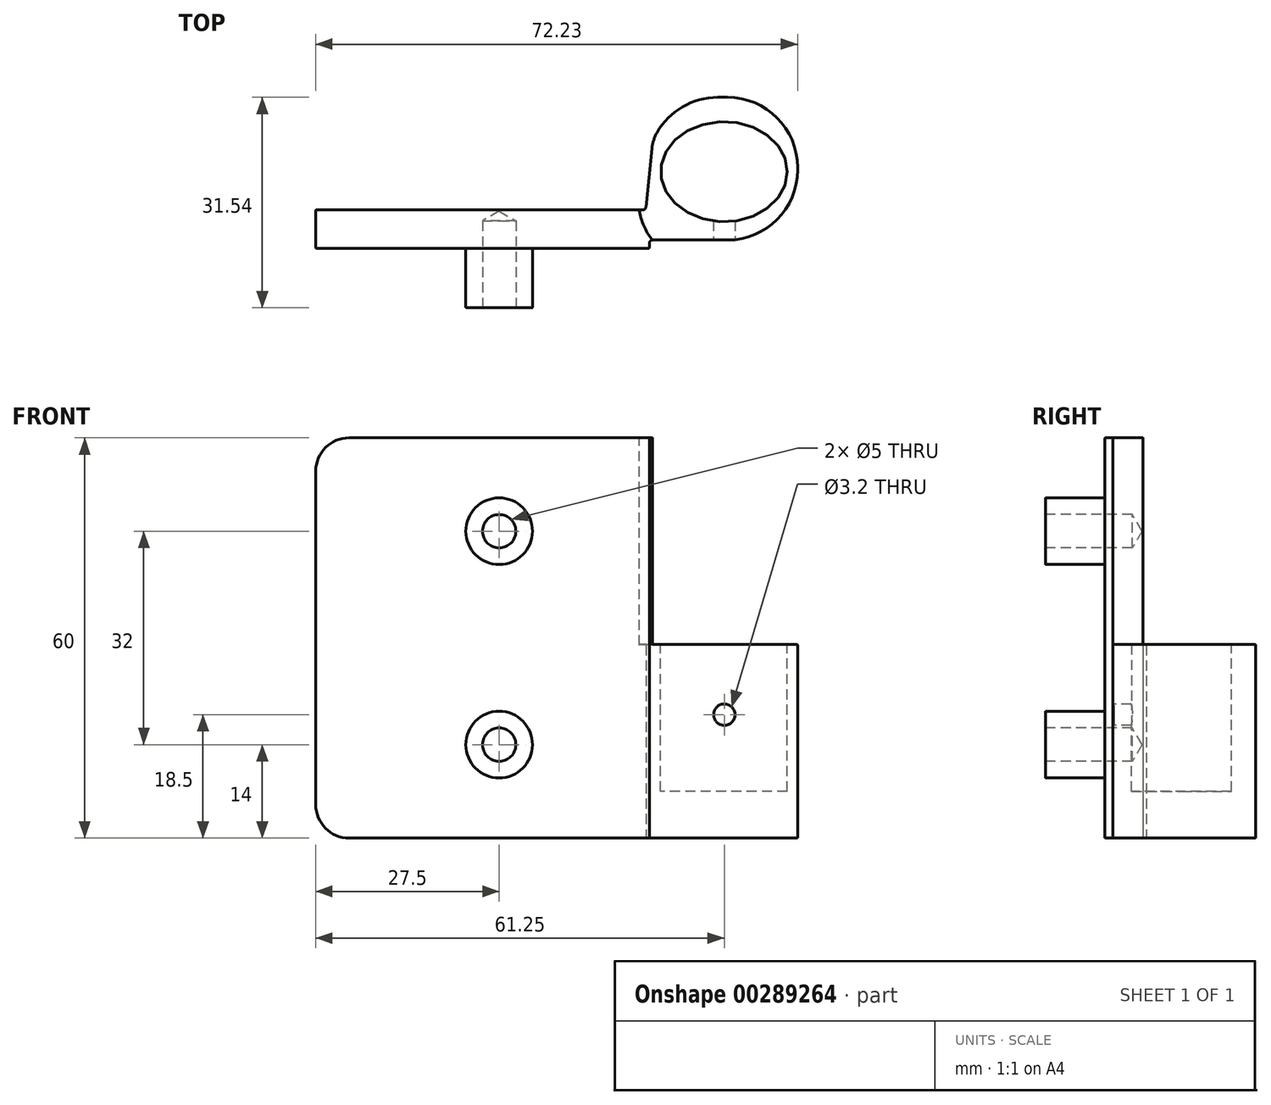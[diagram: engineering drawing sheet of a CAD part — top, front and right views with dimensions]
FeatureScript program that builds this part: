
annotation { "Feature Type Name" : "Feature", "Feature Type Description" : "" }
export const myFeature = defineFeature(function(context is Context, id is Id, definition is map)
    precondition{}
    {
        {
            var Q0;
            Q0=qCreatedBy(makeId("Front.planeOp"),FACE);
            var sketch = newSketch(context, id + "F0", { "sketchPlane" : qUnion([Q0])});
            skLineSegment(sketch, "E0", {"start": v(0, 0) * mm, "end": v(-48.5, 0) * mm});
            skLineSegment(sketch, "E1", {"start": v(-48.5, 0) * mm, "end": v(-48.5, -5.75) * mm});
            skLineSegment(sketch, "E2", {"start": v(-48.5, -5.75) * mm, "end": v(1.5, -5.75) * mm});
            skLineSegment(sketch, "E3", {"start": v(1.5, -5.75) * mm, "end": v(1.5, -5) * mm});
            skLineSegment(sketch, "E4", {"start": v(2, -4.5) * mm, "end": v(3.23, -4.5) * mm});
            skLineSegment(sketch, "E5", {"start": v(3.23, -4.5) * mm, "end": v(13.23, -4.5) * mm});
            skLineSegment(sketch, "E6", {"start": v(23.73, 6) * mm, "end": v(23.73, 6.4) * mm});
            skLineSegment(sketch, "E7", {"start": v(13.23, 16.9) * mm, "end": v(11.78, 16.9) * mm});
            skLineSegment(sketch, "E8", {"start": v(0.5, 0) * mm, "end": v(0, 0) * mm});
            skArc(sketch, "E9.filletArc", {"start": v(13.23, -4.5) * mm, "mid": v(20.66, -1.43) * mm, "end": v(23.73, 6) * mm});
            skArc(sketch, "E10.filletArc", {"start": v(23.73, 6.4) * mm, "mid": v(20.66, 13.82) * mm, "end": v(13.23, 16.9) * mm});
            skArc(sketch, "E11.filletArc", {"start": v(11.78, 16.9) * mm, "mid": v(6.5, 15.47) * mm, "end": v(2.65, 11.6) * mm});
            skArc(sketch, "E12.filletArc", {"start": v(0.5, 0) * mm, "mid": v(0.85, 0.15) * mm, "end": v(1, 0.5) * mm});
            skPoint(sketch, "E13.visualSharp", {"position": v(1.5, -4.5) * mm});
            skArc(sketch, "E13.filletArc", {"start": v(2, -4.5) * mm, "mid": v(1.65, -4.66) * mm, "end": v(1.5, -5) * mm});
            skLineSegment(sketch, "E14", {"start": v(1, 0.5) * mm, "end": v(1.9, 9.23) * mm});
            skPoint(sketch, "E15.visualSharp", {"position": v(2, 10.22) * mm});
            skArc(sketch, "E15.filletArc", {"start": v(2.65, 11.6) * mm, "mid": v(2.15, 10.45) * mm, "end": v(1.9, 9.23) * mm});
            skSolve(sketch);
        }
        {
            var Q0;
            Q0=makeQuery(id+"F0.imprint","IMPRINT",FACE,{"disambiguationData":[TD([[makeQuery(id+"F0.imprint","IMPRINT",EDGE,{"derivedFrom":sQuery(id+"F0.wireOp",EDGE,"E0")}),1.0]])]});
            extrude(context, id + "F1", {"entities" : qUnion([Q0]), "depth" : 60 * mm});
        }
        {
            var Q0;
            Q0=makeQuery(id+"F1.opExtrude","CAP_EDGE",EDGE,{"disambiguationData":[OSD([sQuery(id+"F0.wireOp",EDGE,"E1")])],"isStart":false});
            var Q1;
            Q1=makeQuery(id+"F1.opExtrude","CAP_EDGE",EDGE,{"disambiguationData":[OSD([sQuery(id+"F0.wireOp",EDGE,"E1")])],"isStart":true});
            fillet(context, id + "F2", {"entities" : qUnion([Q0, Q1]), "radius" : 5 * mm, "tangentPropagation" : true, "allowEdgeOverflow" : false});
        }
        {
            var Q0;
            Q0=makeQuery(id+"F1.opExtrude","SWEPT_FACE",FACE,{"disambiguationData":[OSD([sQuery(id+"F0.wireOp",EDGE,"E4"),sQuery(id+"F0.wireOp",EDGE,"E5")])]});
            var sketch = newSketch(context, id + "F3", { "sketchPlane" : qUnion([Q0])});
            skLineSegment(sketch, "E16.bottom", {"start": v(2, 60) * mm, "end": v(31.94, 60) * mm});
            skLineSegment(sketch, "E16.top", {"start": v(2, 29) * mm, "end": v(31.94, 29) * mm});
            skLineSegment(sketch, "E16.left", {"start": v(2, 60) * mm, "end": v(2, 29) * mm});
            skLineSegment(sketch, "E16.right", {"start": v(31.94, 60) * mm, "end": v(31.94, 29) * mm});
            skSolve(sketch);
        }
        {
            var Q0;
            Q0 = qSketchRegion(id + "F3", true);
            extrude(context, id + "F4", {"entities" : qUnion([Q0]), "operationType" : NewBodyOperationType.REMOVE, "endBound" : BoundingType.THROUGH_ALL, "oppositeDirection" : true, "depth" : 25 * mm});
        }
        {
            var Q0;
            Q0=makeQuery(id+"F1.opExtrude","CAP_FACE",FACE,{"disambiguationData":[OSD([sQuery(id+"F0.wireOp",EDGE,"E0"),sQuery(id+"F0.wireOp",EDGE,"E1"),sQuery(id+"F0.wireOp",EDGE,"E2"),sQuery(id+"F0.wireOp",EDGE,"E3"),sQuery(id+"F0.wireOp",EDGE,"E4"),sQuery(id+"F0.wireOp",EDGE,"E5"),sQuery(id+"F0.wireOp",EDGE,"E6"),sQuery(id+"F0.wireOp",EDGE,"E7"),sQuery(id+"F0.wireOp",EDGE,"GG9Xp7Lx-0V8L-KjhP-dehT-RjXL1Wiv3JEy"),sQuery(id+"F0.wireOp",EDGE,"E8"),sQuery(id+"F0.wireOp",EDGE,"E9.filletArc"),sQuery(id+"F0.wireOp",EDGE,"E10.filletArc"),sQuery(id+"F0.wireOp",EDGE,"E11.filletArc"),sQuery(id+"F0.wireOp",EDGE,"E12.filletArc"),sQuery(id+"F0.wireOp",EDGE,"E13.filletArc")])],"isStart":false});
            var sketch = newSketch(context, id + "F5", { "sketchPlane" : qUnion([Q0])});
            skArc(sketch, "E17", {"start": v(0, 0) * mm, "mid": v(0.68, -2.4) * mm, "end": v(2, -4.5) * mm});
            skLineSegment(sketch, "E18", {"start": v(2, -4.5) * mm, "end": v(4.6, -0.03) * mm});
            skLineSegment(sketch, "E19", {"start": v(4.6, -0.03) * mm, "end": v(2.71, 13.2) * mm});
            skLineSegment(sketch, "E20", {"start": v(2.71, 13.2) * mm, "end": v(-1.4, 7.63) * mm});
            skLineSegment(sketch, "E21", {"start": v(0, 0) * mm, "end": v(-1.4, 7.63) * mm});
            skSolve(sketch);
        }
        {
            var Q0;
            Q0 = qSketchRegion(id + "F5", true);
            extrude(context, id + "F6", {"entities" : qUnion([Q0]), "operationType" : NewBodyOperationType.REMOVE, "oppositeDirection" : true, "depth" : 31 * mm});
        }
        {
            var Q0;
            Q0=makeQuery(id+"F1.opExtrude","SWEPT_BODY",BODY,{"disambiguationData":[OSD([sQuery(id+"F0.wireOp",EDGE,"E0"),sQuery(id+"F0.wireOp",EDGE,"E1"),sQuery(id+"F0.wireOp",EDGE,"E2"),sQuery(id+"F0.wireOp",EDGE,"E3"),sQuery(id+"F0.wireOp",EDGE,"E4"),sQuery(id+"F0.wireOp",EDGE,"E5"),sQuery(id+"F0.wireOp",EDGE,"E6"),sQuery(id+"F0.wireOp",EDGE,"E7"),sQuery(id+"F0.wireOp",EDGE,"GG9Xp7Lx-0V8L-KjhP-dehT-RjXL1Wiv3JEy"),sQuery(id+"F0.wireOp",EDGE,"E8"),sQuery(id+"F0.wireOp",EDGE,"E9.filletArc"),sQuery(id+"F0.wireOp",EDGE,"E10.filletArc"),sQuery(id+"F0.wireOp",EDGE,"E11.filletArc"),sQuery(id+"F0.wireOp",EDGE,"E12.filletArc"),sQuery(id+"F0.wireOp",EDGE,"E13.filletArc")])]});
            var Q1;
            Q1=makeQuery(id+"F1.opExtrude","CAP_EDGE",EDGE,{"disambiguationData":[OSD([sQuery(id+"F0.wireOp",EDGE,"E0"),sQuery(id+"F0.wireOp",EDGE,"E8")])],"isStart":true});
            transform(context, id + "F7", {"entities" : qUnion([Q0]), "transformType" : TransformType.ROTATION, "transformAxis" : qUnion([Q1]), "angle" : 90 * degree, "makeCopy" : false});
        }
        {
            var Q0;
            Q0=makeQuery(id+"F1.opExtrude","SWEPT_FACE",FACE,{"disambiguationData":[OSD([sQuery(id+"F0.wireOp",EDGE,"E2")])]});
            var sketch = newSketch(context, id + "F8", { "sketchPlane" : qUnion([Q0])});
            skCircle(sketch, "E22", {"center": v(-21, 46) * mm, "radius": 5 * mm});
            skCircle(sketch, "E23", {"center": v(-21, 14) * mm, "radius": 5 * mm});
            skSolve(sketch);
        }
        {
            var Q0;
            Q0 = qSketchRegion(id + "F8", true);
            extrude(context, id + "F9", {"entities" : qUnion([Q0]), "operationType" : NewBodyOperationType.ADD, "depth" : 8.9 * mm});
        }
        {
            var Q0;
            Q0=makeQuery(id+"F9.opExtrude","CAP_FACE",FACE,{"disambiguationData":[OSD([sQuery(id+"F8.wireOp",EDGE,"E22")])],"isStart":false});
            var sketch = newSketch(context, id + "F10", { "sketchPlane" : qUnion([Q0])});
            skCircle(sketch, "E24", {"center": v(-21, 46) * mm, "radius": 2.5 * mm});
            skSolve(sketch);
        }
        {
            var Q0;
            Q0=makeQuery(id+"F9.opExtrude","CAP_FACE",FACE,{"disambiguationData":[OSD([sQuery(id+"F8.wireOp",EDGE,"E23")])],"isStart":false});
            var sketch = newSketch(context, id + "F11", { "sketchPlane" : qUnion([Q0])});
            skCircle(sketch, "E25", {"center": v(-21, 14) * mm, "radius": 2.5 * mm});
            skSolve(sketch);
        }
        {
            var Q0;
            Q0=sQuery(id+"F10.wireOp",VERTEX,"E24.center");
            var Q1;
            Q1=makeQuery(id+"F1.opExtrude","SWEPT_BODY",BODY,{"disambiguationData":[OSD([sQuery(id+"F0.wireOp",EDGE,"E0"),sQuery(id+"F0.wireOp",EDGE,"E1"),sQuery(id+"F0.wireOp",EDGE,"E2"),sQuery(id+"F0.wireOp",EDGE,"E3"),sQuery(id+"F0.wireOp",EDGE,"E4"),sQuery(id+"F0.wireOp",EDGE,"E5"),sQuery(id+"F0.wireOp",EDGE,"E6"),sQuery(id+"F0.wireOp",EDGE,"E7"),sQuery(id+"F0.wireOp",EDGE,"GG9Xp7Lx-0V8L-KjhP-dehT-RjXL1Wiv3JEy"),sQuery(id+"F0.wireOp",EDGE,"E8"),sQuery(id+"F0.wireOp",EDGE,"E9.filletArc"),sQuery(id+"F0.wireOp",EDGE,"E10.filletArc"),sQuery(id+"F0.wireOp",EDGE,"E11.filletArc"),sQuery(id+"F0.wireOp",EDGE,"E12.filletArc"),sQuery(id+"F0.wireOp",EDGE,"E13.filletArc")])]});
            hole(context, id + "F12", {"style" : HoleStyle.SIMPLE, "endStyle" : HoleEndStyle.BLIND, "standardTappedOrClearance" : lookupTablePath({ "standard" : "ISO", "engagement" : "75%", "pitch" : "1 mm", "size" : "M6", "type" : "Tapped" }), "standardBlindInLast" : lookupTablePath({ "standard" : "ISO", "engagement" : "75%", "pitch" : "1 mm", "size" : "M6", "type" : "Tapped" }), "holeDiameter" : 5 * mm, "showTappedDepth" : true, "holeDepth" : 13 * mm, "tappedDepth" : 10 * mm, "tapClearance" : 3, "locations" : qUnion([Q0]), "scope" : qUnion([Q1]), "majorDiameter" : 6 * mm});
        }
        {
            var Q0;
            Q0=sQuery(id+"F11.wireOp",VERTEX,"E25.center");
            var Q1;
            Q1=makeQuery(id+"F1.opExtrude","SWEPT_BODY",BODY,{"disambiguationData":[OSD([sQuery(id+"F0.wireOp",EDGE,"E0"),sQuery(id+"F0.wireOp",EDGE,"E1"),sQuery(id+"F0.wireOp",EDGE,"E2"),sQuery(id+"F0.wireOp",EDGE,"E3"),sQuery(id+"F0.wireOp",EDGE,"E4"),sQuery(id+"F0.wireOp",EDGE,"E5"),sQuery(id+"F0.wireOp",EDGE,"E6"),sQuery(id+"F0.wireOp",EDGE,"E7"),sQuery(id+"F0.wireOp",EDGE,"GG9Xp7Lx-0V8L-KjhP-dehT-RjXL1Wiv3JEy"),sQuery(id+"F0.wireOp",EDGE,"E8"),sQuery(id+"F0.wireOp",EDGE,"E9.filletArc"),sQuery(id+"F0.wireOp",EDGE,"E10.filletArc"),sQuery(id+"F0.wireOp",EDGE,"E11.filletArc"),sQuery(id+"F0.wireOp",EDGE,"E12.filletArc"),sQuery(id+"F0.wireOp",EDGE,"E13.filletArc")])]});
            hole(context, id + "F13", {"style" : HoleStyle.SIMPLE, "endStyle" : HoleEndStyle.BLIND, "standardTappedOrClearance" : lookupTablePath({ "standard" : "ISO", "engagement" : "75%", "pitch" : "1 mm", "size" : "M6", "type" : "Tapped" }), "standardBlindInLast" : lookupTablePath({ "standard" : "ISO", "engagement" : "75%", "pitch" : "1 mm", "size" : "M6", "type" : "Tapped" }), "holeDiameter" : 5 * mm, "showTappedDepth" : true, "holeDepth" : 13 * mm, "tappedDepth" : 10 * mm, "tapClearance" : 3, "locations" : qUnion([Q0]), "scope" : qUnion([Q1]), "majorDiameter" : 6 * mm});
        }
        {
            var Q0;
            Q0=makeQuery(id+"F6.boolean.opBoolean","MERGE",FACE,{"derivedFrom":[makeQuery(id+"F4.boolean.opBoolean","COPY",FACE,{"derivedFrom":makeQuery(id+"F4.opExtrude","SWEPT_FACE",FACE,{"disambiguationData":[OSD([sQuery(id+"F3.wireOp",EDGE,"E16.top")])]})}),makeQuery(id+"F6.opExtrude","CAP_FACE",FACE,{"disambiguationData":[OSD([sQuery(id+"F5.wireOp",EDGE,"E17"),sQuery(id+"F5.wireOp",EDGE,"E18"),sQuery(id+"F5.wireOp",EDGE,"E19"),sQuery(id+"F5.wireOp",EDGE,"E20"),sQuery(id+"F5.wireOp",EDGE,"E21")])],"isStart":false})]});
            var sketch = newSketch(context, id + "F14", { "sketchPlane" : qUnion([Q0])});
            skEllipse(sketch, "E26", {"center": v(12.7, 5.75) * mm, "majorRadius": 9.5 * mm, "minorRadius": 7.5 * mm, "majorAxis": v(1, 0)});
            skSolve(sketch);
        }
        {
            var Q0;
            Q0 = qSketchRegion(id + "F14", true);
            extrude(context, id + "F15", {"entities" : qUnion([Q0]), "operationType" : NewBodyOperationType.REMOVE, "oppositeDirection" : true, "depth" : 22 * mm});
        }
        {
            var Q0;
            Q0=makeQuery(id+"F1.opExtrude","SWEPT_FACE",FACE,{"disambiguationData":[OSD([sQuery(id+"F0.wireOp",EDGE,"E4"),sQuery(id+"F0.wireOp",EDGE,"E5")])]});
            var sketch = newSketch(context, id + "F16", { "sketchPlane" : qUnion([Q0])});
            skCircle(sketch, "E27", {"center": v(12.75, 18.5) * mm, "radius": 1.5 * mm});
            skSolve(sketch);
        }
        {
            var Q0;
            Q0=sQuery(id+"F16.wireOp",VERTEX,"E27.center");
            var Q1;
            Q1=makeQuery(id+"F1.opExtrude","SWEPT_BODY",BODY,{"disambiguationData":[OSD([sQuery(id+"F0.wireOp",EDGE,"E0"),sQuery(id+"F0.wireOp",EDGE,"E1"),sQuery(id+"F0.wireOp",EDGE,"E2"),sQuery(id+"F0.wireOp",EDGE,"E3"),sQuery(id+"F0.wireOp",EDGE,"E4"),sQuery(id+"F0.wireOp",EDGE,"E5"),sQuery(id+"F0.wireOp",EDGE,"E6"),sQuery(id+"F0.wireOp",EDGE,"E7"),sQuery(id+"F0.wireOp",EDGE,"E8"),sQuery(id+"F0.wireOp",EDGE,"E9.filletArc"),sQuery(id+"F0.wireOp",EDGE,"E10.filletArc"),sQuery(id+"F0.wireOp",EDGE,"E11.filletArc"),sQuery(id+"F0.wireOp",EDGE,"E12.filletArc"),sQuery(id+"F0.wireOp",EDGE,"E13.filletArc"),sQuery(id+"F0.wireOp",EDGE,"E14"),sQuery(id+"F0.wireOp",EDGE,"E15.filletArc")])]});
            hole(context, id + "F17", {"style" : HoleStyle.SIMPLE, "endStyle" : HoleEndStyle.BLIND, "standardTappedOrClearance" : lookupTablePath({ "standard" : "ISO", "engagement" : "75%", "pitch" : "0.75 mm", "size" : "M4", "type" : "Tapped" }), "standardBlindInLast" : lookupTablePath({ "standard" : "ISO", "engagement" : "75%", "pitch" : "0.75 mm", "size" : "M4", "type" : "Tapped" }), "holeDiameter" : 3.2 * mm, "showTappedDepth" : true, "holeDepth" : 12.25 * mm, "tappedDepth" : 10 * mm, "tapClearance" : 3, "locations" : qUnion([Q0]), "scope" : qUnion([Q1])});
        }
        {
            var Q0;
            Q0=makeQuery(id+"F15.boolean.opBoolean","COPY",EDGE,{"derivedFrom":makeQuery(id+"F15.opExtrude","CAP_EDGE",EDGE,{"disambiguationData":[OSD([sQuery(id+"F14.wireOp",EDGE,"E26")])],"isStart":true})});
            var Q1;
            Q1=makeQuery(id+"F6.boolean.opBoolean","INTERSECT",EDGE,{"derivedFrom":[makeQuery(id+"F1.opExtrude","SWEPT_FACE",FACE,{"disambiguationData":[OSD([sQuery(id+"F0.wireOp",EDGE,"E12.filletArc")])]}),makeQuery(id+"F6.opExtrude","CAP_FACE",FACE,{"disambiguationData":[OSD([sQuery(id+"F5.wireOp",EDGE,"E17"),sQuery(id+"F5.wireOp",EDGE,"E18"),sQuery(id+"F5.wireOp",EDGE,"E19"),sQuery(id+"F5.wireOp",EDGE,"E20"),sQuery(id+"F5.wireOp",EDGE,"E21")])],"isStart":false})]});
            var Q2;
            Q2=makeQuery(id+"F6.boolean.opBoolean","INTERSECT",EDGE,{"derivedFrom":[makeQuery(id+"F1.opExtrude","SWEPT_FACE",FACE,{"disambiguationData":[OSD([sQuery(id+"F0.wireOp",EDGE,"E14")])]}),makeQuery(id+"F6.opExtrude","CAP_FACE",FACE,{"disambiguationData":[OSD([sQuery(id+"F5.wireOp",EDGE,"E17"),sQuery(id+"F5.wireOp",EDGE,"E18"),sQuery(id+"F5.wireOp",EDGE,"E19"),sQuery(id+"F5.wireOp",EDGE,"E20"),sQuery(id+"F5.wireOp",EDGE,"E21")])],"isStart":false})]});
            var Q3;
            Q3=makeQuery(id+"F1.opExtrude","CAP_EDGE",EDGE,{"disambiguationData":[OSD([sQuery(id+"F0.wireOp",EDGE,"E0"),sQuery(id+"F0.wireOp",EDGE,"E8")])],"isStart":false});
            var Q4;
            Q4=makeQuery(id+"F1.opExtrude","CAP_EDGE",EDGE,{"disambiguationData":[OSD([sQuery(id+"F0.wireOp",EDGE,"E2")])],"isStart":false});
            var Q5;
            Q5=makeQuery(id+"F1.opExtrude","CAP_EDGE",EDGE,{"disambiguationData":[OSD([sQuery(id+"F0.wireOp",EDGE,"E14")])],"isStart":true});
            var Q6;
            Q6=makeQuery(id+"F1.opExtrude","SWEPT_EDGE",EDGE,{"disambiguationData":[OSD([sQuery(id+"F0.wireOp",EDGE,"E2"),sQuery(id+"F0.wireOp",EDGE,"E3")])]});
            var Q7;
            Q7=makeQuery(id+"F6.boolean.opBoolean","COPY",EDGE,{"derivedFrom":makeQuery(id+"F6.opExtrude","SWEPT_EDGE",EDGE,{"disambiguationData":[OSD([sQuery(id+"F0.wireOp",EDGE,"E0"),sQuery(id+"F0.wireOp",EDGE,"E8"),sQuery(id+"F5.wireOp",EDGE,"E17"),sQuery(id+"F5.wireOp",EDGE,"E21")])]})});
            var Q8;
            Q8=makeQuery(id+"F6.boolean.opBoolean","COPY",EDGE,{"derivedFrom":makeQuery(id+"F6.opExtrude","CAP_EDGE",EDGE,{"disambiguationData":[OSD([sQuery(id+"F5.wireOp",EDGE,"E17")])],"isStart":true})});
            var Q9;
            Q9=makeQuery(id+"F1.opExtrude","CAP_EDGE",EDGE,{"disambiguationData":[OSD([sQuery(id+"F0.wireOp",EDGE,"E13.filletArc")])],"isStart":false});
            var Q10;
            Q10=makeQuery(id+"F9.opExtrude","CAP_EDGE",EDGE,{"disambiguationData":[OSD([sQuery(id+"F8.wireOp",EDGE,"E22")])],"isStart":false});
            var Q11;
            Q11=makeQuery(id+"F9.opExtrude","CAP_EDGE",EDGE,{"disambiguationData":[OSD([sQuery(id+"F8.wireOp",EDGE,"E23")])],"isStart":false});
            var Q12;
            Q12=makeQuery(id+"F9.opExtrude","CAP_EDGE",EDGE,{"disambiguationData":[OSD([sQuery(id+"F8.wireOp",EDGE,"E22")])],"isStart":true});
            var Q13;
            Q13=makeQuery(id+"F9.opExtrude","CAP_EDGE",EDGE,{"disambiguationData":[OSD([sQuery(id+"F8.wireOp",EDGE,"E23")])],"isStart":true});
            fillet(context, id + "F18", {"entities" : qUnion([Q0, Q1, Q2, Q3, Q4, Q5, Q6, Q7, Q8, Q9, Q10, Q11, Q12, Q13]), "radius" : 0.1 * mm, "tangentPropagation" : true, "allowEdgeOverflow" : false});
        }
    });
